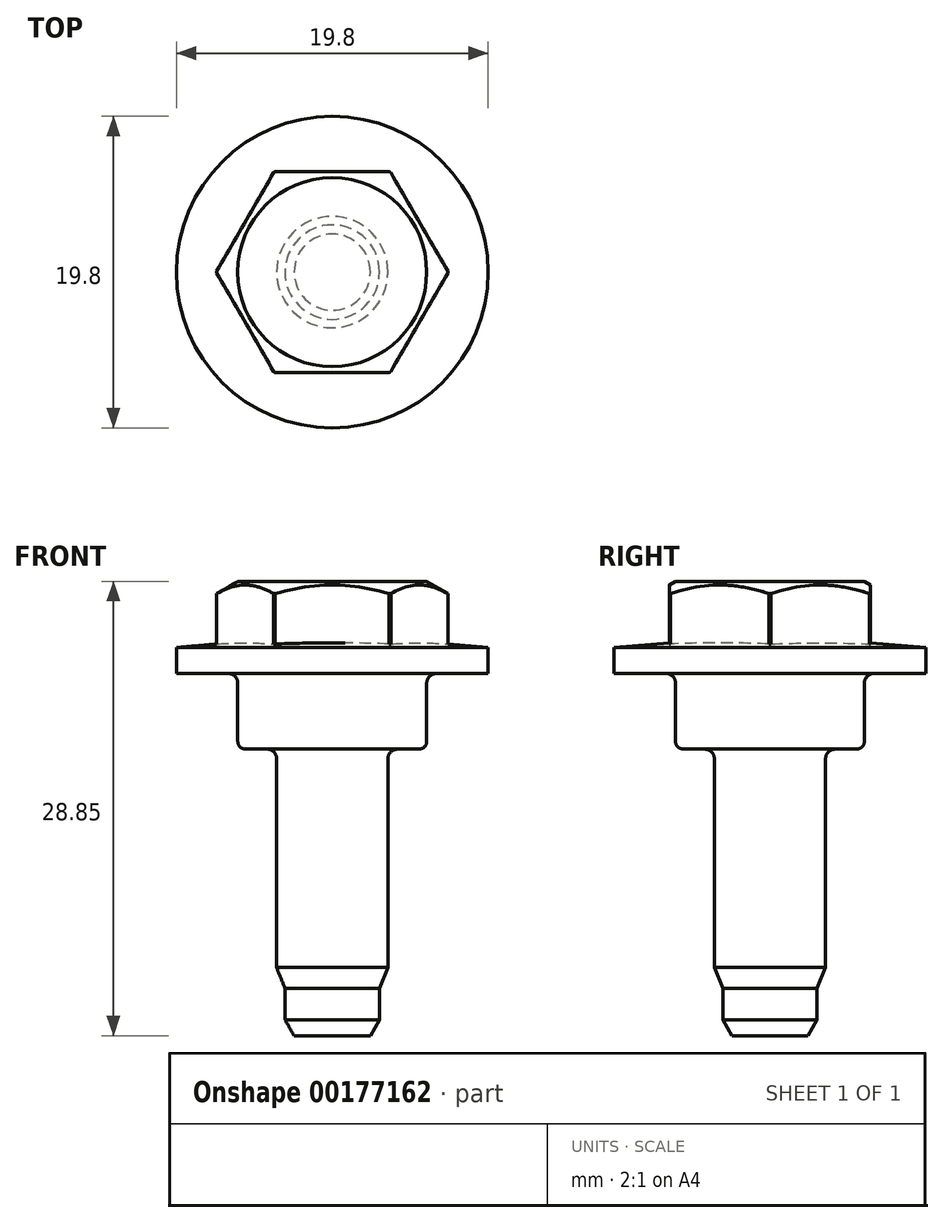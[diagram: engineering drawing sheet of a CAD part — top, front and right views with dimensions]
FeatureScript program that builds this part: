
annotation { "Feature Type Name" : "Feature", "Feature Type Description" : "" }
export const myFeature = defineFeature(function(context is Context, id is Id, definition is map)
    precondition{}
    {
        {
            var Q0;
            Q0=qCreatedBy(makeId("Front.planeOp"),FACE);
            var sketch = newSketch(context, id + "F0", { "sketchPlane" : qUnion([Q0])});
            skLineSegment(sketch, "E0", {"start": v(0, 0) * mm, "end": v(0, 5.85) * mm});
            skLineSegment(sketch, "E1", {"start": v(0, 5.85) * mm, "end": v(6, 5.85) * mm});
            skLineSegment(sketch, "E2", {"start": v(7.34, 5.08) * mm, "end": v(7.34, 1.87) * mm});
            skLineSegment(sketch, "E3", {"start": v(7.34, 1.87) * mm, "end": v(9.9, 1.65) * mm});
            skLineSegment(sketch, "E4", {"start": v(9.9, 1.65) * mm, "end": v(9.9, 0) * mm});
            skLineSegment(sketch, "E5", {"start": v(9.9, 0) * mm, "end": v(6.6, 0) * mm});
            skLineSegment(sketch, "E6", {"start": v(6, 5.85) * mm, "end": v(7.34, 5.08) * mm});
            skLineSegment(sketch, "E7", {"start": v(0, 5.85) * mm, "end": v(0, 0) * mm, "construction": true});
            skLineSegment(sketch, "E8", {"start": v(0, 0) * mm, "end": v(0, -4.8) * mm});
            skLineSegment(sketch, "E9", {"start": v(4.14, -4.8) * mm, "end": v(5.5, -4.8) * mm});
            skLineSegment(sketch, "E10", {"start": v(6, -4.3) * mm, "end": v(6, -0.6) * mm});
            skPoint(sketch, "E11.visualSharp", {"position": v(6, -4.8) * mm});
            skArc(sketch, "E11.filletArc", {"start": v(5.5, -4.8) * mm, "mid": v(5.85, -4.65) * mm, "end": v(6, -4.3) * mm});
            skLineSegment(sketch, "E12", {"start": v(0, -4.8) * mm, "end": v(0, -23) * mm});
            skLineSegment(sketch, "E13", {"start": v(0, -23) * mm, "end": v(2.42, -23) * mm});
            skLineSegment(sketch, "E14", {"start": v(2.42, -23) * mm, "end": v(3, -22) * mm});
            skLineSegment(sketch, "E15", {"start": v(3, -22) * mm, "end": v(3, -20) * mm});
            skLineSegment(sketch, "E16", {"start": v(3, -20) * mm, "end": v(3.54, -18.68) * mm});
            skLineSegment(sketch, "E17", {"start": v(3.54, -18.68) * mm, "end": v(3.54, -5.4) * mm});
            skPoint(sketch, "E18.visualSharp", {"position": v(3.54, -4.8) * mm});
            skArc(sketch, "E18.filletArc", {"start": v(4.14, -4.8) * mm, "mid": v(3.71, -4.98) * mm, "end": v(3.54, -5.4) * mm});
            skPoint(sketch, "E19.visualSharp", {"position": v(6, 0) * mm});
            skArc(sketch, "E19.filletArc", {"start": v(6.6, 0) * mm, "mid": v(6.18, -0.18) * mm, "end": v(6, -0.6) * mm});
            skSolve(sketch);
        }
        {
            var Q0;
            Q0=qSketchRegion(id+"F0",true);
            var Q1;
            Q1=sQuery(id+"F0.wireOp",EDGE,"E0");
            revolve(context, id + "F1", {"entities" : qUnion([Q0]), "axis" : qUnion([Q1]), "revolveType" : RevolveType.FULL});
        }
        {
            var Q0;
            Q0=makeQuery(id+"F1.opRevolve","SWEPT_FACE",FACE,{"disambiguationData":[OSD([sQuery(id+"F0.wireOp",EDGE,"E1")])]});
            var sketch = newSketch(context, id + "F2", { "sketchPlane" : qUnion([Q0])});
            skCircle(sketch, "E20.cCircle", {"center": v(0, 0) * mm, "radius": 6.38 * mm, "construction": true});
            skLineSegment(sketch, "E20.0", {"start": v(-3.69, 6.38) * mm, "end": v(3.69, 6.38) * mm});
            skLineSegment(sketch, "E20.1", {"start": v(3.69, 6.38) * mm, "end": v(7.37, 0) * mm});
            skLineSegment(sketch, "E20.2", {"start": v(7.37, 0) * mm, "end": v(3.69, -6.38) * mm});
            skLineSegment(sketch, "E20.3", {"start": v(3.69, -6.38) * mm, "end": v(-3.69, -6.39) * mm});
            skLineSegment(sketch, "E20.4", {"start": v(-3.69, -6.39) * mm, "end": v(-7.37, 0) * mm});
            skLineSegment(sketch, "E20.5", {"start": v(-7.37, 0) * mm, "end": v(-3.69, 6.39) * mm});
            skPoint(sketch, "E20.0.midPoint", {"position": v(0, 6.38) * mm});
            skCircle(sketch, "E21", {"center": v(0, 0) * mm, "radius": 12.4 * mm});
            skSolve(sketch);
        }
        {
            var Q0;
            Q0=qSketchRegion(id+"F2",true);
            var Q1;
            Q1=makeQuery(id+"F1.opRevolve","SWEPT_FACE",FACE,{"disambiguationData":[OSD([sQuery(id+"F0.wireOp",EDGE,"E3")])]});
            extrude(context, id + "F3", {"entities" : qUnion([Q0]), "operationType" : NewBodyOperationType.REMOVE, "endBound" : BoundingType.UP_TO_SURFACE, "oppositeDirection" : true, "endBoundEntityFace" : qUnion([Q1]), "depth" : 25 * mm, "offsetDistance" : 25 * mm});
        }
    });
